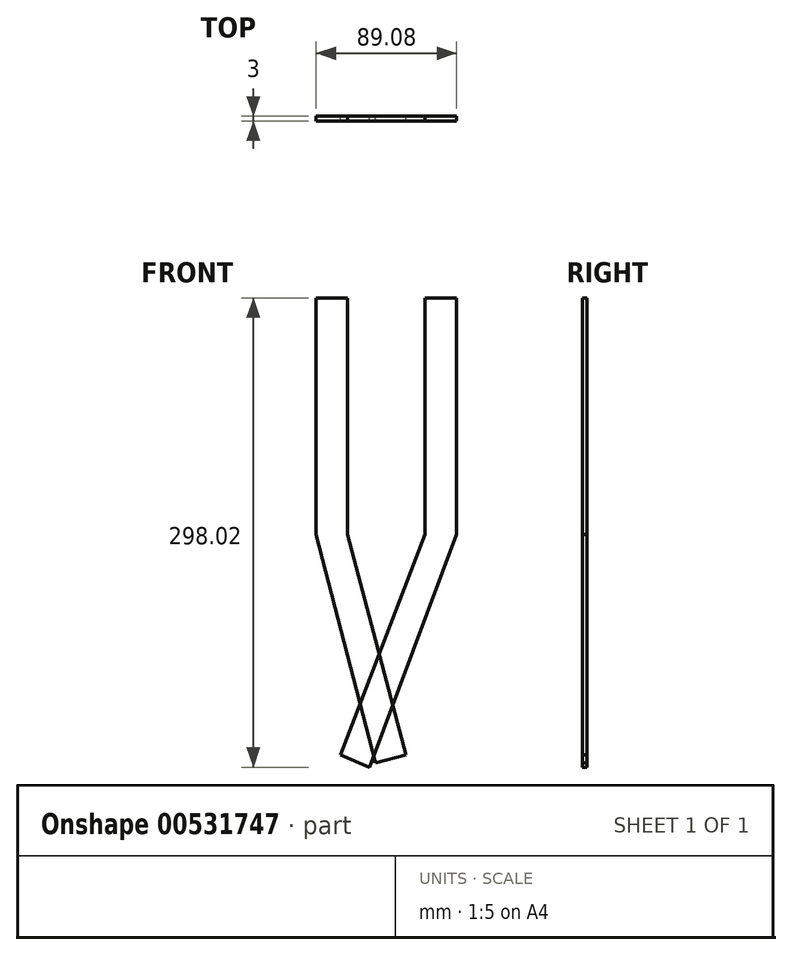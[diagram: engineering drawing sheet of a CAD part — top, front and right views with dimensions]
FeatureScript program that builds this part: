
annotation { "Feature Type Name" : "Feature", "Feature Type Description" : "" }
export const myFeature = defineFeature(function(context is Context, id is Id, definition is map)
    precondition{}
    {
        {
            var Q0;
            Q0=qCreatedBy(makeId("Front.planeOp"),FACE);
            var sketch = newSketch(context, id + "F0", { "sketchPlane" : qUnion([Q0])});
            skLineSegment(sketch, "E0", {"start": v(-41.22, 0) * mm, "end": v(-41.22, 150) * mm});
            skLineSegment(sketch, "E1", {"start": v(-41.22, 0) * mm, "end": v(-3.7, -145.23) * mm});
            skLineSegment(sketch, "E2", {"start": v(-41.22, 150) * mm, "end": v(-21.22, 150) * mm});
            skLineSegment(sketch, "E3", {"start": v(-21.22, 150) * mm, "end": v(-21.22, 0) * mm});
            skLineSegment(sketch, "E4", {"start": v(-3.7, -145.23) * mm, "end": v(15.66, -140.23) * mm});
            skLineSegment(sketch, "E5", {"start": v(15.66, -140.23) * mm, "end": v(-21.22, 0) * mm});
            skSolve(sketch);
        }
        {
            var Q0;
            Q0 = qSketchRegion(id + "F0", true);
            extrude(context, id + "F1", {"entities" : qUnion([Q0]), "depth" : 3 * mm, "offsetDistance" : 25 * mm});
        }
        {
            var Q0;
            Q0=qCreatedBy(makeId("Front.planeOp"),FACE);
            var sketch = newSketch(context, id + "F2", { "sketchPlane" : qUnion([Q0])});
            skLineSegment(sketch, "E6", {"start": v(27.9, 150) * mm, "end": v(27.9, 0) * mm});
            skLineSegment(sketch, "E7", {"start": v(27.9, 0) * mm, "end": v(-25.7, -140.1) * mm});
            skLineSegment(sketch, "E8", {"start": v(27.9, 150) * mm, "end": v(47.86, 150) * mm});
            skLineSegment(sketch, "E9", {"start": v(47.86, 150) * mm, "end": v(47.86, 0) * mm});
            skLineSegment(sketch, "E10", {"start": v(47.86, 0) * mm, "end": v(-7.4, -148.02) * mm});
            skLineSegment(sketch, "E11", {"start": v(-7.4, -148.02) * mm, "end": v(-25.7, -140.1) * mm});
            skSolve(sketch);
        }
        {
            var Q0;
            Q0=makeQuery(id+"F2.imprint","IMPRINT",FACE,{"disambiguationData":[TD([[makeQuery(id+"F2.imprint","IMPRINT",EDGE,{"derivedFrom":sQuery(id+"F2.wireOp",EDGE,"E6")}),1.0]])]});
            extrude(context, id + "F3", {"entities" : qUnion([Q0]), "depth" : 3 * mm, "offsetDistance" : 25 * mm});
        }
    });
